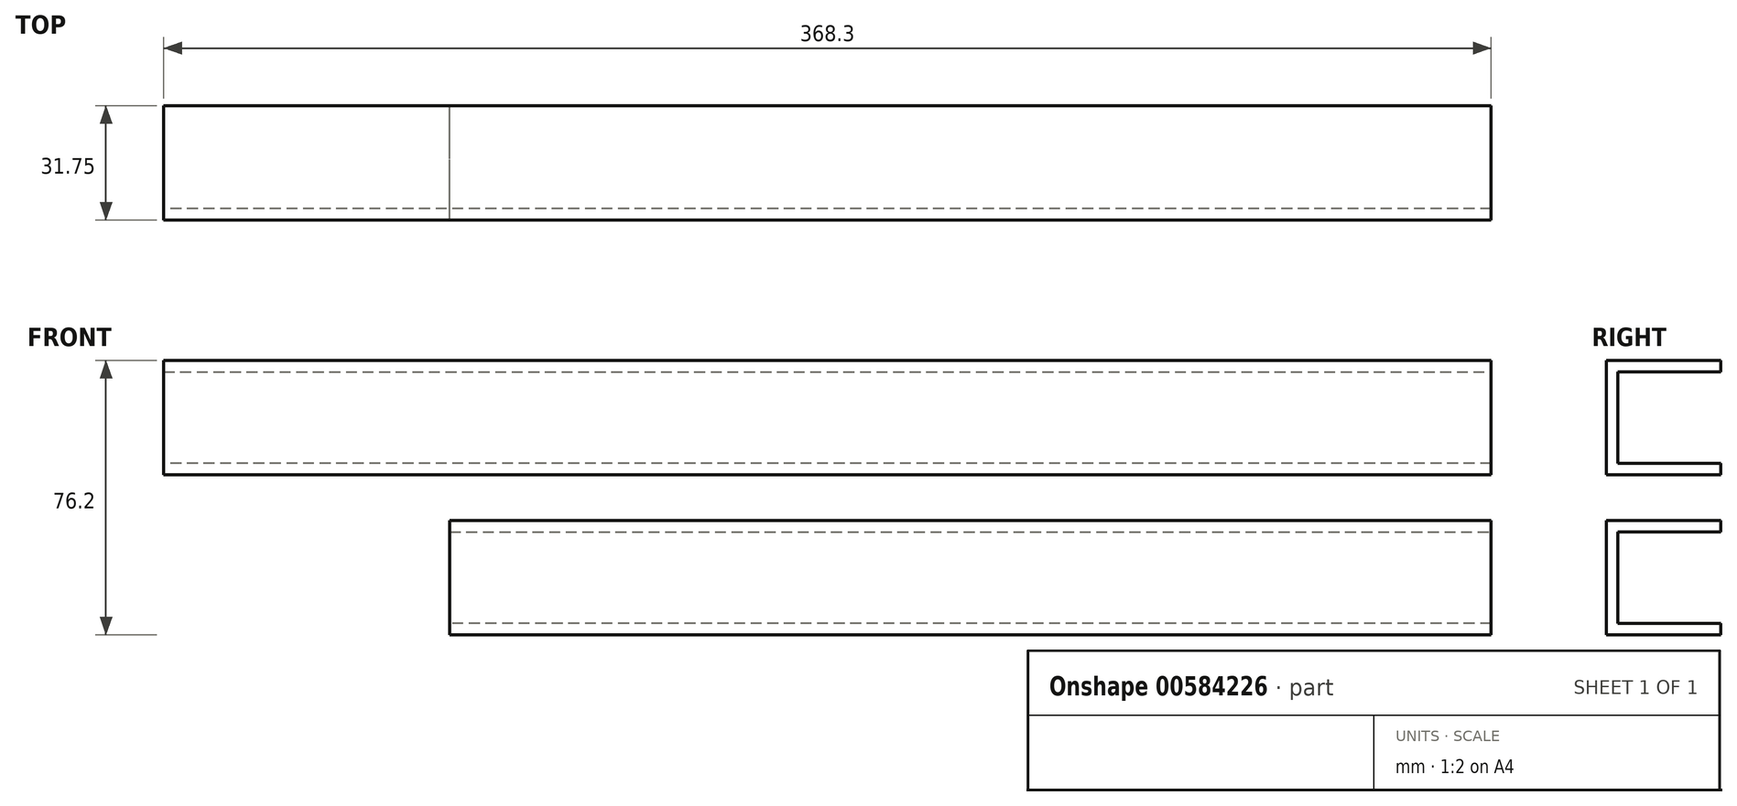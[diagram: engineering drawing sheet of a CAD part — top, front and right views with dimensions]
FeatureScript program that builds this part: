
annotation { "Feature Type Name" : "Feature", "Feature Type Description" : "" }
export const myFeature = defineFeature(function(context is Context, id is Id, definition is map)
    precondition{}
    {
        {
            var Q0;
            Q0=qCreatedBy(makeId("Front.planeOp"),FACE);
            var sketch = newSketch(context, id + "F0", { "sketchPlane" : qUnion([Q0])});
            skLineSegment(sketch, "E0", {"start": v(0, 31.75) * mm, "end": v(-368.3, 31.75) * mm});
            skLineSegment(sketch, "E1", {"start": v(0, 0) * mm, "end": v(0, 31.75) * mm});
            skLineSegment(sketch, "E2", {"start": v(-368.3, 31.75) * mm, "end": v(-368.3, 0) * mm});
            skLineSegment(sketch, "E3", {"start": v(-368.3, 0) * mm, "end": v(0, 0) * mm});
            skLineSegment(sketch, "E4", {"start": v(-368.3, 28.57) * mm, "end": v(0, 28.58) * mm});
            skLineSegment(sketch, "E5", {"start": v(0, 3.18) * mm, "end": v(-368.3, 3.17) * mm});
            skPoint(sketch, "E5.endSnap0", {"position": v(-368.3, 15.88) * mm});
            skSolve(sketch);
        }
        {
            var Q0;
            Q0=makeQuery(id+"F0.imprint","IMPRINT",FACE,{"disambiguationData":[TD([[makeQuery(id+"F0.imprint","IMPRINT",EDGE,{"derivedFrom":sQuery(id+"F0.wireOp",EDGE,"E0")}),1.0]])]});
            var Q1;
            {var subQ0=sQuery(id+"F0.wireOp",EDGE,"E4");Q1=makeQuery(id+"F0.imprint","IMPRINT",FACE,{"disambiguationData":[TD([[makeQuery(id+"F0.imprint","IMPRINT",EDGE,{"derivedFrom":subQ0}),-1.0]])]});}
            var Q2;
            {var subQ0=sQuery(id+"F0.wireOp",EDGE,"E3");Q2=makeQuery(id+"F0.imprint","IMPRINT",FACE,{"disambiguationData":[TD([[makeQuery(id+"F0.imprint","IMPRINT",EDGE,{"derivedFrom":subQ0}),1.0]])]});}
            extrude(context, id + "F1", {"entities" : qUnion([Q0, Q1, Q2]), "depth" : 31.75 * mm, "offsetDistance" : 25.4 * mm});
        }
        {
            var Q0;
            {var subQ0=sQuery(id+"F0.wireOp",EDGE,"E4");Q0=makeQuery(id+"F0.imprint","IMPRINT",FACE,{"disambiguationData":[TD([[makeQuery(id+"F0.imprint","IMPRINT",EDGE,{"derivedFrom":subQ0}),-1.0]])]});}
            extrude(context, id + "F2", {"entities" : qUnion([Q0]), "operationType" : NewBodyOperationType.REMOVE, "oppositeDirection" : true, "depth" : -28.57 * mm, "offsetDistance" : 25.4 * mm});
        }
        {
            var Q0;
            Q0=qCreatedBy(makeId("Front.planeOp"),FACE);
            var sketch = newSketch(context, id + "F3", { "sketchPlane" : qUnion([Q0])});
            skLineSegment(sketch, "E6", {"start": v(0, -12.7) * mm, "end": v(-288.93, -12.7) * mm});
            skLineSegment(sketch, "E7", {"start": v(-288.93, -12.7) * mm, "end": v(-288.93, -44.45) * mm});
            skLineSegment(sketch, "E8", {"start": v(-288.93, -44.45) * mm, "end": v(0, -44.45) * mm});
            skLineSegment(sketch, "E9", {"start": v(0, -44.45) * mm, "end": v(0, -12.7) * mm});
            skLineSegment(sketch, "E10", {"start": v(-288.93, -15.88) * mm, "end": v(0, -15.87) * mm});
            skLineSegment(sketch, "E11", {"start": v(0, -41.28) * mm, "end": v(-288.93, -41.28) * mm});
            skSolve(sketch);
        }
        {
            var Q0;
            {var subQ0=sQuery(id+"F3.wireOp",EDGE,"E10");Q0=makeQuery(id+"F3.imprint","IMPRINT",FACE,{"disambiguationData":[TD([[makeQuery(id+"F3.imprint","IMPRINT",EDGE,{"derivedFrom":subQ0}),-1.0]])]});}
            var Q1;
            {var subQ0=sQuery(id+"F3.wireOp",EDGE,"E6");Q1=makeQuery(id+"F3.imprint","IMPRINT",FACE,{"disambiguationData":[TD([[makeQuery(id+"F3.imprint","IMPRINT",EDGE,{"derivedFrom":subQ0}),1.0]])]});}
            var Q2;
            {var subQ0=sQuery(id+"F3.wireOp",EDGE,"E8");Q2=makeQuery(id+"F3.imprint","IMPRINT",FACE,{"disambiguationData":[TD([[makeQuery(id+"F3.imprint","IMPRINT",EDGE,{"derivedFrom":subQ0}),1.0]])]});}
            extrude(context, id + "F4", {"entities" : qUnion([Q0, Q1, Q2]), "depth" : 31.75 * mm, "offsetDistance" : 25.4 * mm});
        }
        {
            var Q0;
            {var subQ0=sQuery(id+"F3.wireOp",EDGE,"E10");Q0=makeQuery(id+"F3.imprint","IMPRINT",FACE,{"disambiguationData":[TD([[makeQuery(id+"F3.imprint","IMPRINT",EDGE,{"derivedFrom":subQ0}),-1.0]])]});}
            extrude(context, id + "F5", {"entities" : qUnion([Q0]), "operationType" : NewBodyOperationType.REMOVE, "oppositeDirection" : true, "depth" : -28.57 * mm, "offsetDistance" : 25.4 * mm});
        }
    });
